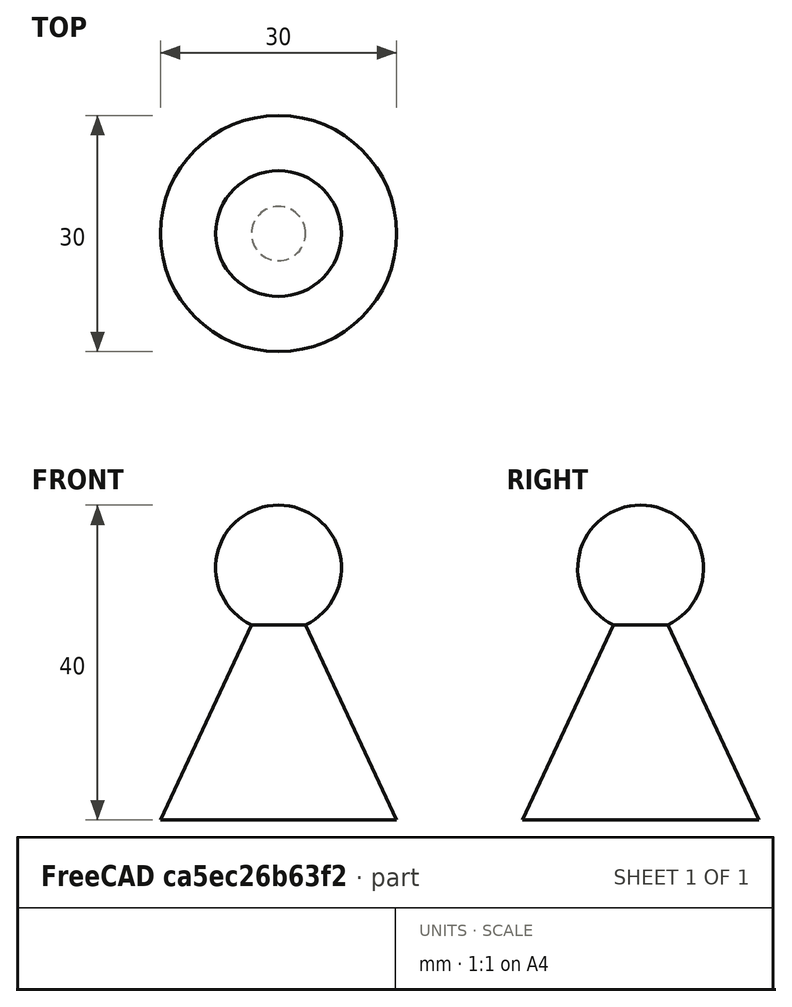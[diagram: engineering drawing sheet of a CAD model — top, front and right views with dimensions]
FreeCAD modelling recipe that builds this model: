
FCSTD DOCUMENT  (FreeCAD 0.17R13217 (Git))
Label: ficha
License: All rights reserved
LicenseURL: http://en.wikipedia.org/wiki/All_rights_reserved
objects: Sketcher::SketchObject×1, PartDesign::Revolution×1, PartDesign::Body×1
note: 4 computed .brp shape members not serialized (recipe doc carries the construction recipe); baked Part::Feature solids carry a one-line shape summary decoded from their .brp

FEATURE [Sketcher::SketchObject] Sketch
  MapMode = 5
  Placement = pos=(0,0,0) rot=(1,0,0;1.5708rad)
  Support = -> [XZ_Plane]
  sketch-geometry (4):
    g0: ArcOfCircle CenterX=0 CenterY=32 CenterZ=0 NormalX=0 NormalY=0 NormalZ=1 AngleXU=0 Radius=8 StartAngle=5.15758 EndAngle=7.85398
    g1: LineSegment StartX=3.44501 StartY=24.7798 StartZ=0 EndX=15 EndY=0 EndZ=0
    g2: LineSegment StartX=15 StartY=0 StartZ=0 EndX=0 EndY=0 EndZ=0
    g3: LineSegment StartX=0 StartY=0 StartZ=0 EndX=0 EndY=40 EndZ=0
  constraints (12):
    c: PointOnObject(g0,g-2)
    c: PointOnObject(g0,g-2)
    c: Coincident(g1,g0)
    c: PointOnObject(g1,g-1)
    c: Coincident(g2,g1)
    c: Coincident(g2,g-1)
    c: Coincident(g3,g-1)
    c: Coincident(g3,g0)
    c: DistanceY(g3,g3) = 40
    c: Radius(g0) = 8
    c: DistanceX(g2,g2) = 15
    c: Angle(g1,g2) = 1.13446
FEATURE [PartDesign::Revolution] Revolution
  Angle = 360
  Axis = (0,0,1)
  Base = (0,0,0)
  Placement = pos=(0,0,0) rot=(1,0,0;1.5708rad)
  Profile = -> Sketch
  ReferenceAxis = -> Sketch [V_Axis]
  Refine = true
FEATURE [PartDesign::Body] Body
  Group = -> [Sketch,Revolution]
  Origin = -> Origin
  Tip = -> Revolution
